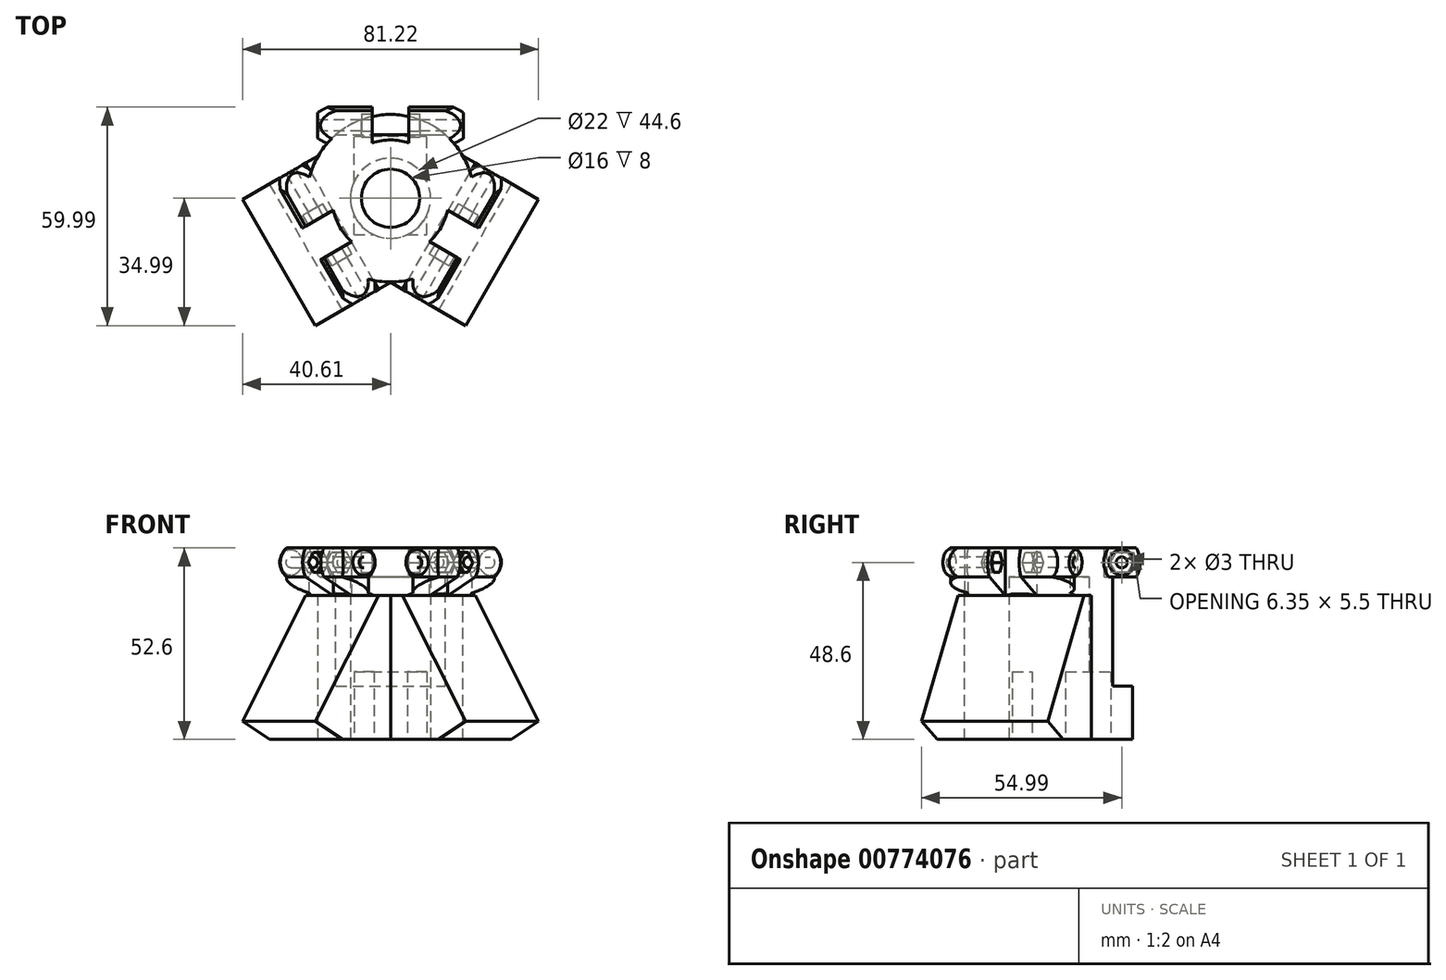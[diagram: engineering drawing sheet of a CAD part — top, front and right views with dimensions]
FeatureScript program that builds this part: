
annotation { "Feature Type Name" : "Feature", "Feature Type Description" : "" }
export const myFeature = defineFeature(function(context is Context, id is Id, definition is map)
    precondition{}
    {
        {
            var Q0;
            Q0=qCreatedBy(makeId("Right.planeOp"),FACE);
            var sketch = newSketch(context, id + "F0", { "sketchPlane" : qUnion([Q0])});
            skLineSegment(sketch, "E0", {"start": v(0, 0) * mm, "end": v(0, 120.63) * mm, "construction": true});
            skSolve(sketch);
        }
        {
            var Q0;
            Q0=qCreatedBy(makeId("Right.planeOp"),FACE);
            var sketch = newSketch(context, id + "F1", { "sketchPlane" : qUnion([Q0])});
            skLineSegment(sketch, "E1", {"start": v(0, 0) * mm, "end": v(41.89, 0) * mm, "construction": true});
            skLineSegment(sketch, "E2.bottom", {"start": v(15, 4) * mm, "end": v(25, 4) * mm});
            skLineSegment(sketch, "E2.top", {"start": v(15, -4) * mm, "end": v(25, -4) * mm});
            skLineSegment(sketch, "E2.left", {"start": v(15, 4) * mm, "end": v(15, -4) * mm});
            skLineSegment(sketch, "E2.right", {"start": v(25, 4) * mm, "end": v(25, -4) * mm});
            skLineSegment(sketch, "E3", {"start": v(20, 6.83) * mm, "end": v(20, -8.7) * mm, "construction": true});
            skCircle(sketch, "E4", {"center": v(20, 0) * mm, "radius": 3.5 * mm});
            skCircle(sketch, "E5.cCircle", {"center": v(20, 0) * mm, "radius": 2.75 * mm, "construction": true});
            skLineSegment(sketch, "E5.0", {"start": v(18.41, 2.75) * mm, "end": v(21.59, 2.75) * mm});
            skLineSegment(sketch, "E5.1", {"start": v(21.59, 2.75) * mm, "end": v(23.18, 0) * mm});
            skLineSegment(sketch, "E5.2", {"start": v(23.18, 0) * mm, "end": v(21.59, -2.75) * mm});
            skLineSegment(sketch, "E5.3", {"start": v(21.59, -2.75) * mm, "end": v(18.41, -2.75) * mm});
            skLineSegment(sketch, "E5.4", {"start": v(18.41, -2.75) * mm, "end": v(16.82, 0) * mm});
            skLineSegment(sketch, "E5.5", {"start": v(16.82, 0) * mm, "end": v(18.41, 2.75) * mm});
            skPoint(sketch, "E5.0.midPoint", {"position": v(20, 2.75) * mm});
            skArc(sketch, "E6", {"start": v(25, 0) * mm, "mid": v(24.75, 2.06) * mm, "end": v(24, 4) * mm});
            skArc(sketch, "E7", {"start": v(16, 4) * mm, "mid": v(15.25, 2.06) * mm, "end": v(15, 0) * mm});
            skArc(sketch, "E8", {"start": v(15, 0) * mm, "mid": v(15.25, -2.06) * mm, "end": v(16, -4) * mm});
            skArc(sketch, "E9", {"start": v(24, -4) * mm, "mid": v(24.75, -2.06) * mm, "end": v(25, 0) * mm});
            skCircle(sketch, "E10", {"center": v(20, 0) * mm, "radius": 1.5 * mm});
            skSolve(sketch);
        }
        {
            var Q0;
            Q0=makeQuery(id+"F1.imprint","IMPRINT",FACE,{"disambiguationData":[TD([[makeQuery(id+"F1.imprint","IMPRINT",EDGE,{"derivedFrom":sQuery(id+"F1.wireOp",EDGE,"E4")}),-1.0]])]});
            var Q1;
            Q1=makeQuery(id+"F1.imprint","IMPRINT",FACE,{"disambiguationData":[TD([[makeQuery(id+"F1.imprint","IMPRINT",EDGE,{"derivedFrom":sQuery(id+"F1.wireOp",EDGE,"E4")}),1.0]])]});
            var Q2;
            Q2=makeQuery(id+"F1.imprint","IMPRINT",FACE,{"disambiguationData":[TD([[makeQuery(id+"F1.imprint","IMPRINT",EDGE,{"derivedFrom":sQuery(id+"F1.wireOp",EDGE,"E5.0")}),-1.0]])]});
            extrude(context, id + "F2", {"entities" : qUnion([Q0, Q1, Q2]), "endBound" : BoundingType.SYMMETRIC, "depth" : 40 * mm, "offsetDistance" : 25 * mm});
        }
        {
            var Q0;
            Q0=makeQuery(id+"F1.imprint","IMPRINT",FACE,{"disambiguationData":[TD([[makeQuery(id+"F1.imprint","IMPRINT",EDGE,{"derivedFrom":sQuery(id+"F1.wireOp",EDGE,"E5.0")}),-1.0]])]});
            extrude(context, id + "F3", {"entities" : qUnion([Q0]), "operationType" : NewBodyOperationType.REMOVE, "endBound" : BoundingType.SYMMETRIC, "oppositeDirection" : true, "depth" : 16 * mm, "offsetDistance" : 25 * mm});
        }
        {
            var Q0;
            Q0=qCreatedBy(makeId("Top.planeOp"),FACE);
            var sketch = newSketch(context, id + "F4", { "sketchPlane" : qUnion([Q0])});
            skLineSegment(sketch, "E11", {"start": v(-32.47, 20) * mm, "end": v(32.89, 20) * mm, "construction": true});
            skArc(sketch, "E12", {"start": v(-20, 16.5) * mm, "mid": v(-16.2, 14.64) * mm, "end": v(-12, 14) * mm});
            skLineSegment(sketch, "E13", {"start": v(-20, 16.5) * mm, "end": v(-20, 14) * mm});
            skLineSegment(sketch, "E14", {"start": v(-20, 14) * mm, "end": v(-12, 14) * mm});
            skLineSegment(sketch, "E15", {"start": v(12, 14) * mm, "end": v(20, 14) * mm});
            skLineSegment(sketch, "E16", {"start": v(20, 14) * mm, "end": v(20, 16.5) * mm});
            skArc(sketch, "E17", {"start": v(12, 14) * mm, "mid": v(16.2, 14.64) * mm, "end": v(20, 16.5) * mm});
            skSolve(sketch);
        }
        {
            var Q0;
            Q0 = qSketchRegion(id + "F4", true);
            var Q1;
            Q1=sQuery(id+"F4.wireOp",EDGE,"E11");
            revolve(context, id + "F5", {"operationType" : NewBodyOperationType.REMOVE, "surfaceOperationType" : NewSurfaceOperationType.NEW, "entities" : qUnion([Q0]), "axis" : qUnion([Q1]), "revolveType" : RevolveType.FULL, "oppositeDirection" : true});
        }
        {
            var Q0;
            Q0=qCreatedBy(makeId("Top.planeOp"),FACE);
            var sketch = newSketch(context, id + "F6", { "sketchPlane" : qUnion([Q0])});
            skLineSegment(sketch, "E18.bottom", {"start": v(-5, 25) * mm, "end": v(5, 25) * mm});
            skLineSegment(sketch, "E18.top", {"start": v(-5, 15) * mm, "end": v(5, 15) * mm});
            skLineSegment(sketch, "E18.left", {"start": v(-5, 25) * mm, "end": v(-5, 15) * mm});
            skLineSegment(sketch, "E18.right", {"start": v(5, 25) * mm, "end": v(5, 15) * mm});
            skPoint(sketch, "E19", {"position": v(0, 15) * mm});
            skSolve(sketch);
        }
        {
            var Q0;
            Q0 = qSketchRegion(id + "F6", true);
            extrude(context, id + "F7", {"entities" : qUnion([Q0]), "operationType" : NewBodyOperationType.REMOVE, "endBound" : BoundingType.SYMMETRIC, "depth" : 25 * mm, "offsetDistance" : 25 * mm});
        }
        {
            var Q0;
            Q0=makeQuery(id+"F2.opExtrude","SWEPT_BODY",BODY,{"disambiguationData":[OSD([sQuery(id+"F1.wireOp",EDGE,"E2.bottom"),sQuery(id+"F1.wireOp",EDGE,"E2.top"),sQuery(id+"F1.wireOp",EDGE,"E6"),sQuery(id+"F1.wireOp",EDGE,"E7"),sQuery(id+"F1.wireOp",EDGE,"E8"),sQuery(id+"F1.wireOp",EDGE,"E9")])]});
            var Q1;
            Q1=sQuery(id+"F0.wireOp",EDGE,"E0");
            circularPattern(context, id + "F8", {"operationType" : NewBodyOperationType.ADD, "entities" : qUnion([Q0]), "axis" : qUnion([Q1]), "angle" : 360 * degree, "instanceCount" : 3, "equalSpace" : true});
        }
        {
            var Q0;
            Q0=qCreatedBy(makeId("Top.planeOp"),FACE);
            var sketch = newSketch(context, id + "F9", { "sketchPlane" : qUnion([Q0])});
            skCircle(sketch, "E20", {"center": v(0, 0) * mm, "radius": 23 * mm});
            skCircle(sketch, "E21", {"center": v(0, 0) * mm, "radius": 16 * mm});
            skCircle(sketch, "E22", {"center": v(0, 0) * mm, "radius": 8 * mm});
            skLineSegment(sketch, "E23", {"start": v(16.02, 16.5) * mm, "end": v(-16.02, 16.5) * mm});
            skLineSegment(sketch, "E24", {"start": v(-5, 16.5) * mm, "end": v(-5, 15.2) * mm});
            skLineSegment(sketch, "E25", {"start": v(5, 16.5) * mm, "end": v(5, 15.2) * mm});
            skLineSegment(sketch, "E26.1.0", {"start": v(6.28, -22.13) * mm, "end": v(22.3, 5.63) * mm});
            skLineSegment(sketch, "E26.1.1", {"start": v(11.79, -12.58) * mm, "end": v(10.66, -11.93) * mm});
            skLineSegment(sketch, "E26.1.2", {"start": v(16.79, -3.92) * mm, "end": v(15.66, -3.27) * mm});
            skLineSegment(sketch, "E26.2.0", {"start": v(-22.3, 5.63) * mm, "end": v(-6.28, -22.13) * mm});
            skLineSegment(sketch, "E26.2.1", {"start": v(-16.79, -3.92) * mm, "end": v(-15.66, -3.27) * mm});
            skLineSegment(sketch, "E26.2.2", {"start": v(-11.79, -12.58) * mm, "end": v(-10.66, -11.93) * mm});
            skLineSegment(sketch, "E26.anchor1", {"start": v(0, 0) * mm, "end": v(-16.02, 16.5) * mm, "construction": true});
            skLineSegment(sketch, "E26.anchor2", {"start": v(0, 0) * mm, "end": v(-6.28, -22.13) * mm, "construction": true});
            skSolve(sketch);
        }
        {
            var Q0;
            {var subQ0=sQuery(id+"F9.wireOp",EDGE,"E25");Q0=makeQuery(id+"F9.imprint","IMPRINT",FACE,{"disambiguationData":[TD([[makeQuery(id+"F9.imprint","IMPRINT",EDGE,{"derivedFrom":subQ0}),1.0]])]});}
            var Q1;
            {var subQ0=sQuery(id+"F9.wireOp",EDGE,"E24");Q1=makeQuery(id+"F9.imprint","IMPRINT",FACE,{"disambiguationData":[TD([[makeQuery(id+"F9.imprint","IMPRINT",EDGE,{"derivedFrom":subQ0}),-1.0]])]});}
            var Q2;
            {var subQ0=sQuery(id+"F9.wireOp",EDGE,"E26.1.1");Q2=makeQuery(id+"F9.imprint","IMPRINT",FACE,{"disambiguationData":[TD([[makeQuery(id+"F9.imprint","IMPRINT",EDGE,{"derivedFrom":subQ0}),1.0]])]});}
            var Q3;
            Q3=makeQuery(id+"F9.imprint","IMPRINT",FACE,{"disambiguationData":[TD([[makeQuery(id+"F9.imprint","IMPRINT",EDGE,{"derivedFrom":sQuery(id+"F9.wireOp",EDGE,"E22")}),-1.0]])]});
            extrude(context, id + "F10", {"entities" : qUnion([Q0, Q1, Q2, Q3]), "operationType" : NewBodyOperationType.ADD, "endBound" : BoundingType.SYMMETRIC, "oppositeDirection" : true, "depth" : 8 * mm, "offsetDistance" : 25 * mm});
        }
        {
            var Q0;
            Q0=qCreatedBy(makeId("Front.planeOp"),FACE);
            var sketch = newSketch(context, id + "F11", { "sketchPlane" : qUnion([Q0])});
            skLineSegment(sketch, "E27", {"start": v(0, 0) * mm, "end": v(0, 96.71) * mm, "construction": true});
            skSolve(sketch);
        }
        {
            var Q0;
            Q0=sQuery(id+"F11.wireOp",EDGE,"E27");
            cPlane(context, id + "F12", {"entities" : qUnion([Q0]), "cplaneType" : CPlaneType.LINE_ANGLE, "offset" : 25 * mm, "angle" : 60 * degree, "width" : 150 * mm, "height" : 150 * mm});
        }
        {
            var Q0;
            Q0=sQuery(id+"F11.wireOp",EDGE,"E27");
            cPlane(context, id + "F13", {"entities" : qUnion([Q0]), "cplaneType" : CPlaneType.LINE_ANGLE, "offset" : 25 * mm, "angle" : 60 * degree, "oppositeDirection" : true, "width" : 150 * mm, "height" : 150 * mm});
        }
        {
            var Q0;
            Q0=qCreatedBy(id+"F13.planeOp",FACE);
            var sketch = newSketch(context, id + "F14", { "sketchPlane" : qUnion([Q0])});
            skLineSegment(sketch, "E28", {"start": v(-24, -4) * mm, "end": v(0, -4) * mm});
            skLineSegment(sketch, "E29", {"start": v(0, -4) * mm, "end": v(0, -48.6) * mm});
            skLineSegment(sketch, "E30", {"start": v(-35.34, -43.64) * mm, "end": v(-15.34, -9) * mm});
            skLineSegment(sketch, "E31", {"start": v(-15.34, -9) * mm, "end": v(-24, -4) * mm});
            skLineSegment(sketch, "E32", {"start": v(-35.34, -43.64) * mm, "end": v(-26.75, -48.6) * mm});
            skLineSegment(sketch, "E33", {"start": v(-26.75, -48.6) * mm, "end": v(0, -48.6) * mm});
            skSolve(sketch);
        }
        {
            var Q0;
            Q0 = qSketchRegion(id + "F14", true);
            extrude(context, id + "F15", {"entities" : qUnion([Q0]), "operationType" : NewBodyOperationType.ADD, "endBound" : BoundingType.SYMMETRIC, "depth" : 40 * mm, "offsetDistance" : 25 * mm});
        }
        {
            var Q0;
            Q0=qCreatedBy(id+"F12.planeOp",FACE);
            var sketch = newSketch(context, id + "F16", { "sketchPlane" : qUnion([Q0])});
            skLineSegment(sketch, "E34", {"start": v(0, -4) * mm, "end": v(-24, -4) * mm});
            skLineSegment(sketch, "E35", {"start": v(-24, -4) * mm, "end": v(-15.34, -9) * mm});
            skLineSegment(sketch, "E36", {"start": v(-15.34, -9) * mm, "end": v(-35.34, -43.64) * mm});
            skLineSegment(sketch, "E37", {"start": v(0, -48.6) * mm, "end": v(0, -4) * mm});
            skLineSegment(sketch, "E38", {"start": v(-35.34, -43.64) * mm, "end": v(-26.75, -48.6) * mm});
            skLineSegment(sketch, "E39", {"start": v(-26.75, -48.6) * mm, "end": v(0, -48.6) * mm});
            skSolve(sketch);
        }
        {
            var Q0;
            Q0 = qSketchRegion(id + "F16", true);
            extrude(context, id + "F17", {"entities" : qUnion([Q0]), "operationType" : NewBodyOperationType.ADD, "endBound" : BoundingType.SYMMETRIC, "depth" : 40 * mm, "offsetDistance" : 25 * mm});
        }
        {
            var Q0;
            {var subQ2=makeQuery(id+"F2.opExtrude","SWEPT_FACE",FACE,{"disambiguationData":[OSD([sQuery(id+"F1.wireOp",EDGE,"E2.top")])]});var subQ3=makeQuery(id+"F7.boolean.opBoolean","SPLIT",FACE,{"disambiguationData":[TD([makeQuery(id+"F5.boolean.opBoolean","COPY",FACE,{"derivedFrom":makeQuery(id+"F5.opRevolve","SWEPT_FACE",FACE,{"disambiguationData":[OSD([sQuery(id+"F4.wireOp",EDGE,"E17")])]})})])],"derivedFrom":subQ2});var subQ4=makeQuery(id+"F7.boolean.opBoolean","SPLIT",FACE,{"disambiguationData":[TD([makeQuery(id+"F5.boolean.opBoolean","COPY",FACE,{"derivedFrom":makeQuery(id+"F5.opRevolve","SWEPT_FACE",FACE,{"disambiguationData":[OSD([sQuery(id+"F4.wireOp",EDGE,"E12")])]})})])],"derivedFrom":subQ2});Q0=makeQuery(id+"F10.boolean.opBoolean","MERGE",FACE,{"derivedFrom":[subQ4,subQ3,makeQuery(id+"F8.opPattern","COPY",FACE,{"derivedFrom":subQ4,"instanceName":"1"}),makeQuery(id+"F8.opPattern","COPY",FACE,{"derivedFrom":subQ3,"instanceName":"1"}),makeQuery(id+"F8.opPattern","COPY",FACE,{"derivedFrom":subQ4,"instanceName":"2"}),makeQuery(id+"F8.opPattern","COPY",FACE,{"derivedFrom":subQ3,"instanceName":"2"}),makeQuery(id+"F10.opExtrude","CAP_FACE",FACE,{"disambiguationData":[OSD([sQuery(id+"F9.wireOp",EDGE,"E20"),sQuery(id+"F9.wireOp",EDGE,"E21"),sQuery(id+"F9.wireOp",EDGE,"E22"),sQuery(id+"F9.wireOp",EDGE,"E23"),sQuery(id+"F9.wireOp",EDGE,"E24"),sQuery(id+"F9.wireOp",EDGE,"E25"),sQuery(id+"F9.wireOp",EDGE,"E26.1.0"),sQuery(id+"F9.wireOp",EDGE,"E26.1.1"),sQuery(id+"F9.wireOp",EDGE,"E26.1.2"),sQuery(id+"F9.wireOp",EDGE,"E26.2.0"),sQuery(id+"F9.wireOp",EDGE,"E26.2.1"),sQuery(id+"F9.wireOp",EDGE,"E26.2.2")])],"isStart":false})]});}
            var sketch = newSketch(context, id + "F18", { "sketchPlane" : qUnion([Q0])});
            skLineSegment(sketch, "E40.bottom", {"start": v(-15, -17.44) * mm, "end": v(15, -17.44) * mm});
            skLineSegment(sketch, "E40.top", {"start": v(-15, -3.18) * mm, "end": v(15, -3.18) * mm});
            skLineSegment(sketch, "E40.left", {"start": v(-15, -17.44) * mm, "end": v(-15, -3.18) * mm});
            skLineSegment(sketch, "E40.right", {"start": v(15, -17.44) * mm, "end": v(15, -3.18) * mm});
            skCircle(sketch, "E41", {"center": v(0, 0) * mm, "radius": 23 * mm});
            skPoint(sketch, "E42", {"position": v(0, -17.44) * mm});
            skLineSegment(sketch, "E43", {"start": v(0, 0) * mm, "end": v(0, -28.74) * mm, "construction": true});
            skSolve(sketch);
        }
        {
            var Q0;
            {var subQ0=sQuery(id+"F18.wireOp",EDGE,"E41");var subQ1=sQuery(id+"F18.wireOp",EDGE,"E40.left");var subQ2=makeQuery(id+"F18.imprint","INTERSECT",VERTEX,{"derivedFrom":[sQuery(id+"F18.wireOp",EDGE,"E40.bottom"),subQ1,subQ0]});var subQ5=makeQuery(id+"F2.opExtrude","SWEPT_FACE",FACE,{"disambiguationData":[OSD([sQuery(id+"F1.wireOp",EDGE,"E2.top")])]});var subQ8=makeQuery(id+"F5.opRevolve","SWEPT_FACE",FACE,{"disambiguationData":[OSD([sQuery(id+"F4.wireOp",EDGE,"E12")])]});var subQ13=makeQuery(id+"F18.imprint","INTERSECT",VERTEX,{"derivedFrom":[makeQuery(id+"F5.boolean.opBoolean","INTERSECT",EDGE,{"derivedFrom":[subQ5,subQ8]}),subQ0]});Q0=makeQuery(id+"F18.imprint","IMPRINT",FACE,{"disambiguationData":[TD([[makeQuery(id+"F18.imprint","IMPRINT",EDGE,{"disambiguationData":[TD([[subQ13,-1.0],[subQ2,1.0]])],"derivedFrom":subQ0}),1.0]])]});}
            var Q1;
            {var subQ0=sQuery(id+"F18.wireOp",EDGE,"E41");var subQ1=sQuery(id+"F18.wireOp",EDGE,"E40.right");var subQ2=makeQuery(id+"F18.imprint","INTERSECT",VERTEX,{"derivedFrom":[sQuery(id+"F18.wireOp",EDGE,"E40.bottom"),subQ1,subQ0]});var subQ5=makeQuery(id+"F5.opRevolve","SWEPT_FACE",FACE,{"disambiguationData":[OSD([sQuery(id+"F4.wireOp",EDGE,"E17")])]});var subQ6=makeQuery(id+"F2.opExtrude","SWEPT_FACE",FACE,{"disambiguationData":[OSD([sQuery(id+"F1.wireOp",EDGE,"E2.top")])]});var subQ13=makeQuery(id+"F18.imprint","INTERSECT",VERTEX,{"derivedFrom":[makeQuery(id+"F5.boolean.opBoolean","INTERSECT",EDGE,{"derivedFrom":[subQ6,subQ5]}),subQ0]});Q1=makeQuery(id+"F18.imprint","IMPRINT",FACE,{"disambiguationData":[TD([[makeQuery(id+"F18.imprint","IMPRINT",EDGE,{"disambiguationData":[TD([[subQ13,1.0],[subQ2,-1.0]])],"derivedFrom":subQ0}),1.0]])]});}
            var Q2;
            {var subQ1=sQuery(id+"F9.wireOp",EDGE,"E24");var subQ8=sQuery(id+"F9.wireOp",EDGE,"E21");var subQ9=makeQuery(id+"F10.opExtrude","CAP_EDGE",EDGE,{"disambiguationData":[OSD([subQ8]),TDD([makeQuery(id+"F9.imprint","IMPRINT",EDGE,{"disambiguationData":[TD([[makeQuery(id+"F9.imprint","INTERSECT",VERTEX,{"derivedFrom":[subQ8,subQ1]}),1.0]])],"derivedFrom":subQ8})])],"isStart":false});Q2=makeQuery(id+"F18.imprint","IMPRINT",FACE,{"disambiguationData":[TD([[makeQuery(id+"F18.imprint","IMPRINT",EDGE,{"derivedFrom":subQ9}),1.0]])]});}
            var Q3;
            {var subQ24=sQuery(id+"F18.wireOp",EDGE,"E40.top");Q3=makeQuery(id+"F18.imprint","IMPRINT",FACE,{"disambiguationData":[TD([[makeQuery(id+"F18.imprint","IMPRINT",EDGE,{"derivedFrom":subQ24}),-1.0]])]});}
            var Q4;
            {var subQ1=sQuery(id+"F18.wireOp",EDGE,"E40.top");Q4=makeQuery(id+"F18.imprint","IMPRINT",FACE,{"disambiguationData":[TD([[makeQuery(id+"F18.imprint","IMPRINT",EDGE,{"derivedFrom":subQ1}),1.0]])]});}
            var Q5;
            {var subQ0=sQuery(id+"F9.wireOp",EDGE,"E24");var subQ5=sQuery(id+"F9.wireOp",EDGE,"E21");var subQ7=makeQuery(id+"F10.opExtrude","CAP_EDGE",EDGE,{"disambiguationData":[OSD([subQ5]),TDD([makeQuery(id+"F9.imprint","IMPRINT",EDGE,{"disambiguationData":[TD([[makeQuery(id+"F9.imprint","INTERSECT",VERTEX,{"derivedFrom":[subQ5,subQ0]}),1.0]])],"derivedFrom":subQ5})])],"isStart":false});Q5=makeQuery(id+"F18.imprint","IMPRINT",FACE,{"disambiguationData":[TD([[makeQuery(id+"F18.imprint","IMPRINT",EDGE,{"derivedFrom":subQ7}),-1.0]])]});}
            extrude(context, id + "F19", {"entities" : qUnion([Q0, Q1, Q2, Q3, Q4, Q5]), "operationType" : NewBodyOperationType.ADD, "depth" : (50 - 4.4 - 1) * mm, "offsetDistance" : 25 * mm});
        }
        {
            var Q0;
            {var subQ6=makeQuery(id+"F5.boolean.opBoolean","COPY",FACE,{"derivedFrom":makeQuery(id+"F5.opRevolve","SWEPT_FACE",FACE,{"disambiguationData":[OSD([sQuery(id+"F4.wireOp",EDGE,"E17")])]})});var subQ12=sQuery(id+"F14.wireOp",EDGE,"E28");Q0=makeQuery(id+"F15.boolean.opBoolean","SPLIT",FACE,{"disambiguationData":[TD([makeQuery(id+"F8.opPattern","COPY",FACE,{"derivedFrom":subQ6,"instanceName":"1"})])],"derivedFrom":makeQuery(id+"F15.opExtrude","SWEPT_FACE",FACE,{"disambiguationData":[OSD([subQ12])]})});}
            var Q1;
            {var subQ1=sQuery(id+"F14.wireOp",EDGE,"E28");var subQ7=makeQuery(id+"F5.boolean.opBoolean","COPY",FACE,{"derivedFrom":makeQuery(id+"F5.opRevolve","SWEPT_FACE",FACE,{"disambiguationData":[OSD([sQuery(id+"F4.wireOp",EDGE,"E12")])]})});Q1=makeQuery(id+"F17.boolean.opBoolean","MERGE",FACE,{"derivedFrom":[makeQuery(id+"F15.boolean.opBoolean","SPLIT",FACE,{"disambiguationData":[TD([makeQuery(id+"F8.opPattern","COPY",FACE,{"derivedFrom":subQ7,"instanceName":"1"})])],"derivedFrom":makeQuery(id+"F15.opExtrude","SWEPT_FACE",FACE,{"disambiguationData":[OSD([subQ1])]})}),makeQuery(id+"F17.opExtrude","SWEPT_FACE",FACE,{"disambiguationData":[OSD([sQuery(id+"F16.wireOp",EDGE,"E34")])]})]});}
            var Q2;
            {var subQ4=sQuery(id+"F16.wireOp",EDGE,"E34");var subQ9=makeQuery(id+"F2.opExtrude","SWEPT_FACE",FACE,{"disambiguationData":[OSD([sQuery(id+"F1.wireOp",EDGE,"E2.top")])]});Q2=makeQuery(id+"F17.boolean.opBoolean","SPLIT",FACE,{"disambiguationData":[TD([subQ9])],"derivedFrom":makeQuery(id+"F17.opExtrude","SWEPT_FACE",FACE,{"disambiguationData":[OSD([subQ4])]})});}
            var Q3;
            {var subQ5=makeQuery(id+"F7.opExtrude","SWEPT_FACE",FACE,{"disambiguationData":[OSD([sQuery(id+"F6.wireOp",EDGE,"E18.left")])]});Q3=makeQuery(id+"F17.boolean.opBoolean","SPLIT",FACE,{"disambiguationData":[TD([makeQuery(id+"F8.opPattern","COPY",FACE,{"derivedFrom":makeQuery(id+"F7.boolean.opBoolean","COPY",FACE,{"derivedFrom":subQ5}),"instanceName":"2"})])],"derivedFrom":makeQuery(id+"F17.opExtrude","SWEPT_FACE",FACE,{"disambiguationData":[OSD([sQuery(id+"F16.wireOp",EDGE,"E34")])]})});}
            var Q4;
            {var subQ4=makeQuery(id+"F7.opExtrude","SWEPT_FACE",FACE,{"disambiguationData":[OSD([sQuery(id+"F6.wireOp",EDGE,"E18.left")])]});Q4=makeQuery(id+"F15.boolean.opBoolean","SPLIT",FACE,{"disambiguationData":[TD([makeQuery(id+"F8.opPattern","COPY",FACE,{"derivedFrom":makeQuery(id+"F7.boolean.opBoolean","COPY",FACE,{"derivedFrom":subQ4}),"instanceName":"1"})])],"derivedFrom":makeQuery(id+"F15.opExtrude","SWEPT_FACE",FACE,{"disambiguationData":[OSD([sQuery(id+"F14.wireOp",EDGE,"E28")])]})});}
            extrude(context, id + "F20", {"entities" : qUnion([Q0, Q1, Q2, Q3, Q4]), "operationType" : NewBodyOperationType.REMOVE, "oppositeDirection" : true, "depth" : 5 * mm, "offsetDistance" : 25 * mm});
        }
        {
            var Q0;
            Q0=qCreatedBy(id+"F13.planeOp",FACE);
            var sketch = newSketch(context, id + "F21", { "sketchPlane" : qUnion([Q0])});
            skLineSegment(sketch, "E44", {"start": v(-24, -4) * mm, "end": v(-15.34, -9) * mm});
            skLineSegment(sketch, "E45", {"start": v(-15.34, -9) * mm, "end": v(-24.24, -24.42) * mm});
            skLineSegment(sketch, "E46", {"start": v(-24.24, -24.42) * mm, "end": v(-24, -4) * mm});
            skSolve(sketch);
        }
        {
            var Q0;
            Q0 = qSketchRegion(id + "F21", true);
            extrude(context, id + "F22", {"entities" : qUnion([Q0]), "operationType" : NewBodyOperationType.REMOVE, "endBound" : BoundingType.SYMMETRIC, "oppositeDirection" : true, "depth" : 40 * mm, "offsetDistance" : 25 * mm});
        }
        {
            var Q0;
            Q0=qCreatedBy(id+"F12.planeOp",FACE);
            var sketch = newSketch(context, id + "F23", { "sketchPlane" : qUnion([Q0])});
            skLineSegment(sketch, "E47", {"start": v(-15.34, -9) * mm, "end": v(-25.6, -26.76) * mm});
            skLineSegment(sketch, "E48", {"start": v(-25.6, -26.76) * mm, "end": v(-24, -4) * mm});
            skLineSegment(sketch, "E49", {"start": v(-15.34, -9) * mm, "end": v(-24, -4) * mm});
            skSolve(sketch);
        }
        {
            var Q0;
            Q0 = qSketchRegion(id + "F23", true);
            extrude(context, id + "F24", {"entities" : qUnion([Q0]), "operationType" : NewBodyOperationType.REMOVE, "endBound" : BoundingType.SYMMETRIC, "oppositeDirection" : true, "depth" : 40 * mm, "offsetDistance" : 25 * mm});
        }
        {
            var Q0;
            Q0=makeQuery(id+"F19.boolean.opBoolean","MERGE",FACE,{"derivedFrom":[makeQuery(id+"F17.boolean.opBoolean","MERGE",FACE,{"derivedFrom":[makeQuery(id+"F15.opExtrude","SWEPT_FACE",FACE,{"disambiguationData":[OSD([sQuery(id+"F14.wireOp",EDGE,"E33")])]}),makeQuery(id+"F17.opExtrude","SWEPT_FACE",FACE,{"disambiguationData":[OSD([sQuery(id+"F16.wireOp",EDGE,"E39")])]})]}),makeQuery(id+"F19.opExtrude","CAP_FACE",FACE,{"disambiguationData":[OSD([sQuery(id+"F18.wireOp",EDGE,"E40.bottom"),sQuery(id+"F18.wireOp",EDGE,"E41")])],"isStart":false})]});
            var sketch = newSketch(context, id + "F25", { "sketchPlane" : qUnion([Q0])});
            skCircle(sketch, "E50", {"center": v(0, 0) * mm, "radius": 23 * mm});
            skSolve(sketch);
        }
        {
            var Q0;
            Q0 = qSketchRegion(id + "F25", true);
            extrude(context, id + "F26", {"entities" : qUnion([Q0]), "operationType" : NewBodyOperationType.ADD, "oppositeDirection" : true, "depth" : (50 - 4.4 - 1 - 30) * mm, "offsetDistance" : 25 * mm});
        }
        {
            var Q0;
            Q0=makeQuery(id+"F19.opExtrude","CAP_FACE",FACE,{"disambiguationData":[OSD([sQuery(id+"F18.wireOp",EDGE,"E40.bottom"),sQuery(id+"F18.wireOp",EDGE,"E41")])],"isStart":false});
            var sketch = newSketch(context, id + "F27", { "sketchPlane" : qUnion([Q0])});
            skCircle(sketch, "E51", {"center": v(0, 0) * mm, "radius": 11 * mm});
            skSolve(sketch);
        }
        {
            var Q0;
            Q0 = qSketchRegion(id + "F27", true);
            extrude(context, id + "F28", {"entities" : qUnion([Q0]), "operationType" : NewBodyOperationType.REMOVE, "oppositeDirection" : true, "depth" : (50 - 4.4 - 1) * mm, "offsetDistance" : 25 * mm});
        }
        {
            var Q0;
            Q0=makeQuery(id+"F26.boolean.opBoolean","MERGE",FACE,{"derivedFrom":[makeQuery(id+"F19.boolean.opBoolean","MERGE",FACE,{"derivedFrom":[makeQuery(id+"F17.boolean.opBoolean","MERGE",FACE,{"derivedFrom":[makeQuery(id+"F15.opExtrude","SWEPT_FACE",FACE,{"disambiguationData":[OSD([sQuery(id+"F14.wireOp",EDGE,"E33")])]}),makeQuery(id+"F17.opExtrude","SWEPT_FACE",FACE,{"disambiguationData":[OSD([sQuery(id+"F16.wireOp",EDGE,"E39")])]})]}),makeQuery(id+"F19.opExtrude","CAP_FACE",FACE,{"disambiguationData":[OSD([sQuery(id+"F18.wireOp",EDGE,"E40.bottom"),sQuery(id+"F18.wireOp",EDGE,"E41")])],"isStart":false})]}),makeQuery(id+"F26.opExtrude","CAP_FACE",FACE,{"disambiguationData":[OSD([sQuery(id+"F25.wireOp",EDGE,"E50")])],"isStart":true})]});
            var sketch = newSketch(context, id + "F29", { "sketchPlane" : qUnion([Q0])});
            skLineSegment(sketch, "E52.bottom", {"start": v(-10, 10) * mm, "end": v(10, 10) * mm});
            skLineSegment(sketch, "E52.top", {"start": v(-10, -17) * mm, "end": v(10, -17) * mm});
            skLineSegment(sketch, "E52.left", {"start": v(-10, 10) * mm, "end": v(-10, -17) * mm});
            skLineSegment(sketch, "E52.right", {"start": v(10, 10) * mm, "end": v(10, -17) * mm});
            skSolve(sketch);
        }
        {
            var Q0;
            Q0 = qSketchRegion(id + "F29", true);
            extrude(context, id + "F30", {"entities" : qUnion([Q0]), "operationType" : NewBodyOperationType.REMOVE, "oppositeDirection" : true, "depth" : (15 + 3.6) * mm, "offsetDistance" : 25 * mm});
        }
    });
